# Revit family: Jardinera Madera
name_source: partatom
category: Furniture
units: mm (PartAtom-declared; Revit-internal decimal feet)

## family parameters
Always vertical = Yes
Cut with Voids When Loaded = No
OmniClass Number = 23.40.20.00
OmniClass Title = General Furniture and Specialties
Room Calculation Point = No
Shared = No
Work Plane-Based = No

## types (5) — shared parameters
Fabricante = BENITO URBAN SL
Ficha_Tecnica = https://www.benito.com
Material = Madera de pino
URL_Producto = https://www.benito.com
zero-valued in all types: Default Elevation

## per-type parameters (varying)
| type | A | B | Description | H | Referencia | Type Comments |
| Jardinera Madera-UM1640-1-1800mm | 1.8 m | 0.6 m | Tablones de madera de pino con tratamiento autoclave a vacio-presión clase 4 contra la carcoma, termitas e insectos. | 0.45 m | UM1640-1 | Anclaje recomendado: Apoyado por su propio peso. |
| Jardinera Madera-UM1640-2-1000mm | 1 m | 0.5 m | Tablones de madera de pino con tratamiento autoclave a vacio-presión clase 4 contra la carcoma, termitas e insectos | 0.45 m | UM1640-2 | Anclaje recomendado: Apoyado por su propio peso. |
| Jardinera Madera-UM1640-4-1000mm | 1 m | 1 m | Tablones de madera de pino con tratamiento autoclave a vacio-presión clase 4 contra la carcoma, termitas e insectos. | 0.655 m | UM1640-4 | Anclaje recomendado: Apoyado por su propio peso |
| Jardinera Madera-UM1640-5-600mm | 0.6 m | 0.6 m | Tablones de madera de pino con tratamiento autoclave a vacio-presión clase 4 contra la carcoma, termitas e insectos | 0.45 m | UM1640-5 | Anclaje recomendado: Apoyado por su propio peso |
| Jardinera Madera-UM1640-6-1000mm | 1 m | 1 m | Tablones de madera de pino con tratamiento autoclave a vacio-presión clase 4 contra la carcoma, termitas e insectos | 1 m | UM1640-6 |  |

type visibility flags: 5 boolean params named "<type name>" — each type sets only its own to Yes (folded from table)

## geometry (parser evidence)
native form markers: Blend x6, Sweep x14
no freeform markers — native parametric forms only
